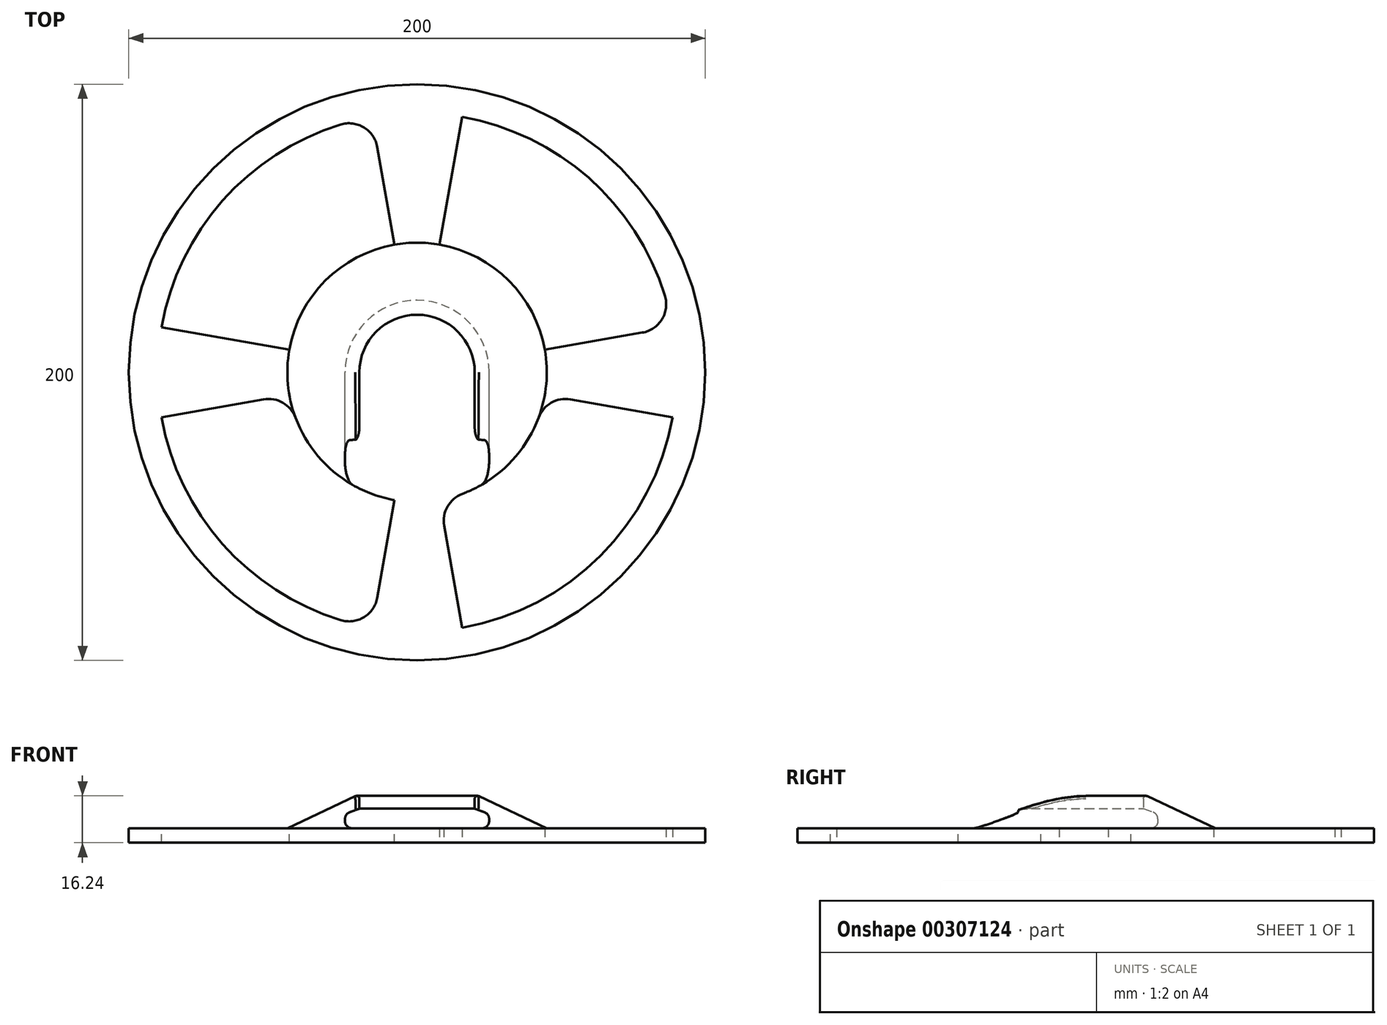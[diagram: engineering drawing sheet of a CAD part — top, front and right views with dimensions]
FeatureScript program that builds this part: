
annotation { "Feature Type Name" : "Feature", "Feature Type Description" : "" }
export const myFeature = defineFeature(function(context is Context, id is Id, definition is map)
    precondition{}
    {
        {
            var Q0;
            Q0=qCreatedBy(makeId("Front.planeOp"),FACE);
            var sketch = newSketch(context, id + "F0", { "sketchPlane" : qUnion([Q0])});
            skLineSegment(sketch, "E0", {"start": v(0, 0) * mm, "end": v(25, 0) * mm});
            skLineSegment(sketch, "E1", {"start": v(45, -5) * mm, "end": v(0, -5) * mm});
            skLineSegment(sketch, "E2", {"start": v(0, -5) * mm, "end": v(0, 0) * mm});
            skPoint(sketch, "E3.orphan", {"position": v(45, 0) * mm});
            skLineSegment(sketch, "E4", {"start": v(25, 0) * mm, "end": v(25, 5) * mm});
            skLineSegment(sketch, "E5", {"start": v(25, 5) * mm, "end": v(20, 6.82) * mm});
            skLineSegment(sketch, "E6", {"start": v(20, 6.82) * mm, "end": v(20, 11.82) * mm});
            skLineSegment(sketch, "E7", {"start": v(20, 11.82) * mm, "end": v(45, 0) * mm});
            skLineSegment(sketch, "E8", {"start": v(45, 0) * mm, "end": v(45, -5) * mm});
            skSolve(sketch);
        }
        {
            var Q0;
            Q0 = qSketchRegion(id + "F0", true);
            var Q1;
            Q1=sQuery(id+"F0.wireOp",EDGE,"E2");
            revolve(context, id + "F1", {"entities" : qUnion([Q0]), "axis" : qUnion([Q1]), "revolveType" : RevolveType.ONE_DIRECTION, "angle" : 360 * degree});
        }
        {
            var Q0;
            Q0=qCreatedBy(makeId("Front.planeOp"),FACE);
            var sketch = newSketch(context, id + "F2", { "sketchPlane" : qUnion([Q0])});
            skLineSegment(sketch, "E9", {"start": v(-20, 6.82) * mm, "end": v(-20, 11.82) * mm});
            skLineSegment(sketch, "E10", {"start": v(20, 11.82) * mm, "end": v(20, 6.82) * mm});
            skLineSegment(sketch, "E11.0.0", {"start": v(-25, 0) * mm, "end": v(25, 0) * mm});
            skLineSegment(sketch, "E12", {"start": v(-25, 0) * mm, "end": v(-25, 5) * mm});
            skLineSegment(sketch, "E13", {"start": v(25, 5) * mm, "end": v(25, 0) * mm});
            skLineSegment(sketch, "E14", {"start": v(-25, 5) * mm, "end": v(-20, 6.82) * mm});
            skLineSegment(sketch, "E15", {"start": v(20, 6.82) * mm, "end": v(25, 5) * mm});
            skLineSegment(sketch, "E16.0", {"start": v(20, 11.82) * mm, "end": v(-20, 11.82) * mm});
            skSolve(sketch);
        }
        {
            var Q0;
            Q0 = qSketchRegion(id + "F2", true);
            extrude(context, id + "F3", {"entities" : qUnion([Q0]), "operationType" : NewBodyOperationType.REMOVE, "endBound" : BoundingType.THROUGH_ALL, "depth" : 25 * mm});
        }
        {
            var Q0;
            Q0=makeQuery(id+"F1.opRevolve","SWEPT_FACE",FACE,{"disambiguationData":[OSD([sQuery(id+"F0.wireOp",EDGE,"E1")])]});
            var sketch = newSketch(context, id + "F4", { "sketchPlane" : qUnion([Q0])});
            skCircle(sketch, "E17", {"center": v(0, 0) * mm, "radius": 100 * mm});
            skCircle(sketch, "E18", {"center": v(0, 0) * mm, "radius": 90 * mm});
            skSolve(sketch);
        }
        {
            var Q0;
            Q0 = qSketchRegion(id + "F4", true);
            extrude(context, id + "F5", {"entities" : qUnion([Q0]), "oppositeDirection" : true, "depth" : 5 * mm});
        }
        {
            var Q0;
            Q0=qCreatedBy(makeId("Front.planeOp"),FACE);
            var sketch = newSketch(context, id + "F6", { "sketchPlane" : qUnion([Q0])});
            skLineSegment(sketch, "E19", {"start": v(0, 0) * mm, "end": v(0, 20) * mm, "construction": true});
            skLineSegment(sketch, "E20", {"start": v(-45, -5) * mm, "end": v(-45, 0) * mm});
            skLineSegment(sketch, "E21", {"start": v(45, 0) * mm, "end": v(45, -5) * mm});
            skLineSegment(sketch, "E22", {"start": v(-90, -5) * mm, "end": v(-90, 0) * mm});
            skLineSegment(sketch, "E23", {"start": v(90, 0) * mm, "end": v(90, -5) * mm});
            skLineSegment(sketch, "E24", {"start": v(-90, 0) * mm, "end": v(-45, 0) * mm});
            skLineSegment(sketch, "E25", {"start": v(-45, -5) * mm, "end": v(-90, -5) * mm});
            skLineSegment(sketch, "E26", {"start": v(90, -5) * mm, "end": v(45, -5) * mm});
            skLineSegment(sketch, "E27", {"start": v(45, 0) * mm, "end": v(90, 0) * mm});
            skSolve(sketch);
        }
        {
            var Q0;
            Q0 = qSketchRegion(id + "F6", true);
            var Q1;
            Q1=sQuery(id+"F6.wireOp",EDGE,"E19");
            revolve(context, id + "F7", {"operationType" : NewBodyOperationType.ADD, "entities" : qUnion([Q0]), "axis" : qUnion([Q1]), "revolveType" : RevolveType.SYMMETRIC, "angle" : 20 * degree});
        }
        {
            var Q0;
            Q0=qCreatedBy(makeId("Right.planeOp"),FACE);
            var sketch = newSketch(context, id + "F8", { "sketchPlane" : qUnion([Q0])});
            skLineSegment(sketch, "E28", {"start": v(0, 0) * mm, "end": v(0, 20) * mm, "construction": true});
            skLineSegment(sketch, "E29", {"start": v(45, 0) * mm, "end": v(45, -5) * mm});
            skLineSegment(sketch, "E30", {"start": v(90, 0) * mm, "end": v(90, -5) * mm});
            skLineSegment(sketch, "E31", {"start": v(45, -5) * mm, "end": v(90, -5) * mm});
            skLineSegment(sketch, "E32", {"start": v(90, 0) * mm, "end": v(45, 0) * mm});
            skLineSegment(sketch, "E33", {"start": v(-45, -5) * mm, "end": v(-45, 0) * mm});
            skLineSegment(sketch, "E34", {"start": v(-90, -5) * mm, "end": v(-90, 0) * mm});
            skLineSegment(sketch, "E35", {"start": v(-45, -5) * mm, "end": v(-90, -5) * mm});
            skLineSegment(sketch, "E36", {"start": v(-90, 0) * mm, "end": v(-45, 0) * mm});
            skSolve(sketch);
        }
        {
            var Q0;
            Q0 = qSketchRegion(id + "F8", true);
            var Q1;
            Q1=sQuery(id+"F8.wireOp",EDGE,"E28");
            revolve(context, id + "F9", {"operationType" : NewBodyOperationType.ADD, "entities" : qUnion([Q0]), "axis" : qUnion([Q1]), "revolveType" : RevolveType.SYMMETRIC, "angle" : 20 * degree});
        }
        {
            var Q0;
            Q0=makeQuery(id+"F1.opRevolve","SWEPT_EDGE",EDGE,{"disambiguationData":[OSD([sQuery(id+"F0.wireOp",EDGE,"E6"),sQuery(id+"F0.wireOp",EDGE,"E7")])]});
            var Q1;
            Q1=makeQuery(id+"F3.boolean.opBoolean","INTERSECT",EDGE,{"derivedFrom":[makeQuery(id+"F1.opRevolve","SWEPT_FACE",FACE,{"disambiguationData":[OSD([sQuery(id+"F0.wireOp",EDGE,"E7")])]}),makeQuery(id+"F3.opExtrude","SWEPT_FACE",FACE,{"disambiguationData":[OSD([sQuery(id+"F2.wireOp",EDGE,"f4a93f66-89c4-4a73-b3e2-17d7893bedb9")])]})]});
            var Q2;
            Q2=makeQuery(id+"F3.boolean.opBoolean","INTERSECT",EDGE,{"derivedFrom":[makeQuery(id+"F1.opRevolve","SWEPT_FACE",FACE,{"disambiguationData":[OSD([sQuery(id+"F0.wireOp",EDGE,"E7")])]}),makeQuery(id+"F3.opExtrude","SWEPT_FACE",FACE,{"disambiguationData":[OSD([sQuery(id+"F2.wireOp",EDGE,"73e09200-8e57-4483-a71f-662178566176")])]})]});
            var Q3;
            Q3=makeQuery(id+"F3.boolean.opBoolean","INTERSECT",EDGE,{"derivedFrom":[makeQuery(id+"F1.opRevolve","SWEPT_FACE",FACE,{"disambiguationData":[OSD([sQuery(id+"F0.wireOp",EDGE,"E7")])]}),makeQuery(id+"F3.opExtrude","SWEPT_FACE",FACE,{"disambiguationData":[OSD([sQuery(id+"F2.wireOp",EDGE,"64aff4ee-1882-473b-a42a-8827de5f9001")])]})]});
            var Q4;
            Q4=makeQuery(id+"F3.boolean.opBoolean","INTERSECT",EDGE,{"derivedFrom":[makeQuery(id+"F1.opRevolve","SWEPT_FACE",FACE,{"disambiguationData":[OSD([sQuery(id+"F0.wireOp",EDGE,"E7")])]}),makeQuery(id+"F3.opExtrude","SWEPT_FACE",FACE,{"disambiguationData":[OSD([sQuery(id+"F2.wireOp",EDGE,"ef642765-d67f-4a50-820b-96f5473efe75")])]})]});
            fillet(context, id + "F10", {"entities" : qUnion([Q0, Q1, Q2, Q3, Q4]), "radius" : 1 * mm, "tangentPropagation" : true, "allowEdgeOverflow" : false});
        }
        {
            var Q0;
            Q0=makeQuery(id+"F1.opRevolve","SWEPT_EDGE",EDGE,{"disambiguationData":[OSD([sQuery(id+"F0.wireOp",EDGE,"E4"),sQuery(id+"F0.wireOp",EDGE,"E5")])]});
            var Q1;
            Q1=makeQuery(id+"F1.opRevolve","SWEPT_EDGE",EDGE,{"disambiguationData":[OSD([sQuery(id+"F0.wireOp",EDGE,"E0"),sQuery(id+"F0.wireOp",EDGE,"E4")])]});
            fillet(context, id + "F11", {"entities" : qUnion([Q0, Q1]), "radius" : 2.5 * mm, "tangentPropagation" : true, "allowEdgeOverflow" : false});
        }
        {
            var Q0;
            Q0=makeQuery(id+"F7.opRevolve","CAP_EDGE",EDGE,{"disambiguationData":[OSD([sQuery(id+"F6.wireOp",EDGE,"E20")]),OD(0.0)],"isStart":false});
            var Q1;
            Q1=makeQuery(id+"F9.opRevolve","CAP_EDGE",EDGE,{"disambiguationData":[OSD([sQuery(id+"F8.wireOp",EDGE,"E33")])],"isStart":true});
            var Q2;
            Q2=makeQuery(id+"F9.opRevolve","CAP_EDGE",EDGE,{"disambiguationData":[OSD([sQuery(id+"F8.wireOp",EDGE,"E33")])],"isStart":false});
            var Q3;
            Q3=makeQuery(id+"F7.opRevolve","CAP_EDGE",EDGE,{"disambiguationData":[OSD([sQuery(id+"F6.wireOp",EDGE,"E21")])],"isStart":true});
            var Q4;
            Q4=makeQuery(id+"F7.opRevolve","CAP_EDGE",EDGE,{"disambiguationData":[OSD([sQuery(id+"F6.wireOp",EDGE,"E21")])],"isStart":false});
            var Q5;
            Q5=makeQuery(id+"F9.opRevolve","CAP_EDGE",EDGE,{"disambiguationData":[OSD([sQuery(id+"F8.wireOp",EDGE,"E29")]),OD(1.0)],"isStart":false});
            var Q6;
            Q6=makeQuery(id+"F9.opRevolve","CAP_EDGE",EDGE,{"disambiguationData":[OSD([sQuery(id+"F8.wireOp",EDGE,"E29")]),OD(0.0)],"isStart":false});
            var Q7;
            Q7=makeQuery(id+"F7.opRevolve","CAP_EDGE",EDGE,{"disambiguationData":[OSD([sQuery(id+"F6.wireOp",EDGE,"E20")]),OD(1.0)],"isStart":false});
            var Q8;
            Q8=makeQuery(id+"F7.opRevolve","CAP_EDGE",EDGE,{"disambiguationData":[OSD([sQuery(id+"F6.wireOp",EDGE,"E22")]),OD(0.0)],"isStart":false});
            var Q9;
            Q9=makeQuery(id+"F7.opRevolve","CAP_EDGE",EDGE,{"disambiguationData":[OSD([sQuery(id+"F6.wireOp",EDGE,"E22")]),OD(1.0)],"isStart":false});
            var Q10;
            Q10=makeQuery(id+"F9.opRevolve","CAP_EDGE",EDGE,{"disambiguationData":[OSD([sQuery(id+"F8.wireOp",EDGE,"E34")])],"isStart":true});
            var Q11;
            Q11=makeQuery(id+"F7.opRevolve","CAP_EDGE",EDGE,{"disambiguationData":[OSD([sQuery(id+"F6.wireOp",EDGE,"E23")])],"isStart":false});
            var Q12;
            Q12=makeQuery(id+"F9.opRevolve","CAP_EDGE",EDGE,{"disambiguationData":[OSD([sQuery(id+"F8.wireOp",EDGE,"E30")]),OD(0.0)],"isStart":false});
            var Q13;
            Q13=makeQuery(id+"F7.opRevolve","CAP_EDGE",EDGE,{"disambiguationData":[OSD([sQuery(id+"F6.wireOp",EDGE,"E23")])],"isStart":true});
            var Q14;
            Q14=makeQuery(id+"F9.opRevolve","CAP_EDGE",EDGE,{"disambiguationData":[OSD([sQuery(id+"F8.wireOp",EDGE,"E34")])],"isStart":false});
            var Q15;
            Q15=makeQuery(id+"F9.opRevolve","CAP_EDGE",EDGE,{"disambiguationData":[OSD([sQuery(id+"F8.wireOp",EDGE,"E30")]),OD(1.0)],"isStart":false});
            fillet(context, id + "F12", {"entities" : qUnion([Q0, Q1, Q2, Q3, Q4, Q5, Q6, Q7, Q8, Q9, Q10, Q11, Q12, Q13, Q14, Q15]), "radius" : 10 * mm, "tangentPropagation" : true, "allowEdgeOverflow" : false});
        }
    });
